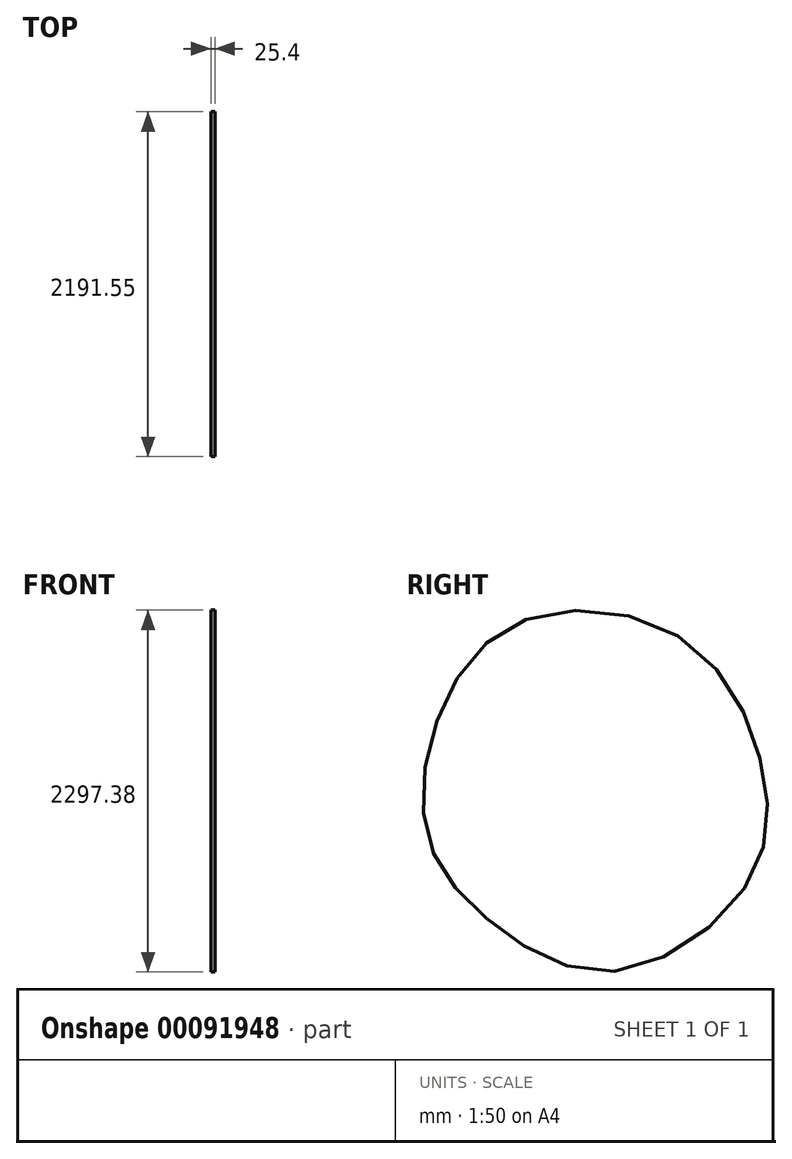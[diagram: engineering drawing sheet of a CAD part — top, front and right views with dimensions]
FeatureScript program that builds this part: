
annotation { "Feature Type Name" : "Feature", "Feature Type Description" : "" }
export const myFeature = defineFeature(function(context is Context, id is Id, definition is map)
    precondition{}
    {
        {
            var Q0;
            Q0=qCreatedBy(makeId("Right.planeOp"),FACE);
            var sketch = newSketch(context, id + "F0", { "sketchPlane" : qUnion([Q0])});
            skFitSpline(sketch, "E0", {"points": [v(261.13, -1501.05) * mm, v(1112.82, -935.52) * mm, v(1198, -192.85) * mm, v(704.09, 604.83) * mm, v(-301.78, 734.62) * mm, v(-842.57, 150.57) * mm, v(-923.7, -649.8) * mm, v(-518.1, -1190.59) * mm, v(261.13, -1501.05) * mm]});
            skSolve(sketch);
        }
        {
            var Q0;
            Q0 = qSketchRegion(id + "F0", true);
            var Q1;
            Q1=makeQuery(id+"F0.imprint","IMPRINT",FACE,{"disambiguationData":[TD([[makeQuery(id+"F0.imprint","IMPRINT",EDGE,{"derivedFrom":sQuery(id+"F0.wireOp",EDGE,"E0")}),1.0]])]});
            extrude(context, id + "F1", {"entities" : qUnion([Q0, Q1]), "depth" : 25.4 * mm});
        }
    });
